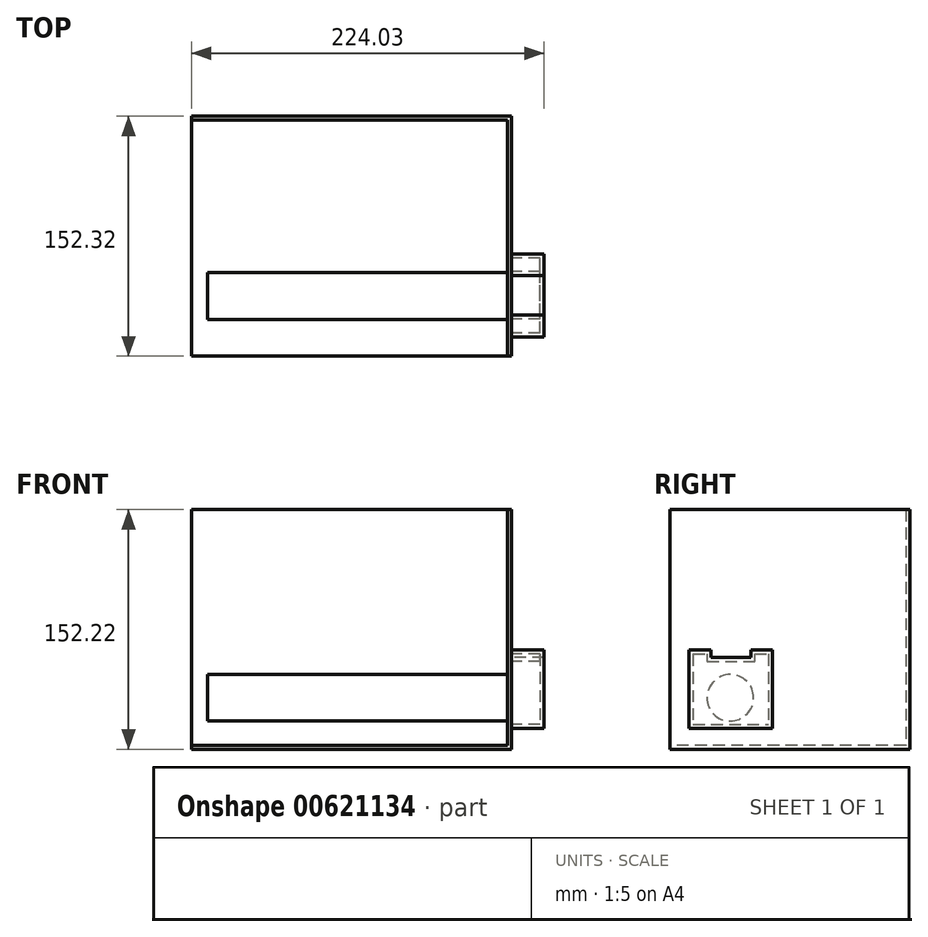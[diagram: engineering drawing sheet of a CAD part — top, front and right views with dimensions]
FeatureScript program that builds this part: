
annotation { "Feature Type Name" : "Feature", "Feature Type Description" : "" }
export const myFeature = defineFeature(function(context is Context, id is Id, definition is map)
    precondition{}
    {
        {
            var Q0;
            Q0=qCreatedBy(makeId("Right.planeOp"),FACE);
            var sketch = newSketch(context, id + "F0", { "sketchPlane" : qUnion([Q0])});
            skLineSegment(sketch, "E0.bottom", {"start": v(76.16, 76.11) * mm, "end": v(-76.16, 76.11) * mm});
            skLineSegment(sketch, "E0.top", {"start": v(76.16, -76.11) * mm, "end": v(-76.16, -76.11) * mm});
            skLineSegment(sketch, "E0.left", {"start": v(76.16, 76.11) * mm, "end": v(76.16, -76.11) * mm});
            skLineSegment(sketch, "E0.right", {"start": v(-76.16, 76.11) * mm, "end": v(-76.16, -76.11) * mm});
            skPoint(sketch, "E0.middle", {"position": v(0, 0) * mm});
            skSolve(sketch);
        }
        {
            var Q0;
            Q0 = qSketchRegion(id + "F0", true);
            extrude(context, id + "F1", {"entities" : qUnion([Q0]), "oppositeDirection" : true, "depth" : 203.2 * mm, "offsetDistance" : 25.4 * mm});
        }
        {
            var Q0;
            Q0=makeQuery(id+"F1.opExtrude","CAP_FACE",FACE,{"disambiguationData":[OSD([sQuery(id+"F0.wireOp",EDGE,"E0.bottom"),sQuery(id+"F0.wireOp",EDGE,"E0.top"),sQuery(id+"F0.wireOp",EDGE,"E0.left"),sQuery(id+"F0.wireOp",EDGE,"E0.right")])],"isStart":true});
            var sketch = newSketch(context, id + "F2", { "sketchPlane" : qUnion([Q0])});
            skLineSegment(sketch, "E1.top", {"start": v(-64.17, -62.88) * mm, "end": v(-11.2, -62.88) * mm});
            skLineSegment(sketch, "E1.left", {"start": v(-64.17, -13.06) * mm, "end": v(-64.17, -62.88) * mm});
            skLineSegment(sketch, "E1.right", {"start": v(-11.2, -13.06) * mm, "end": v(-11.2, -62.88) * mm});
            skLineSegment(sketch, "E2", {"start": v(-64.17, -13.06) * mm, "end": v(-50.1, -13.06) * mm});
            skLineSegment(sketch, "E3", {"start": v(-50.1, -13.06) * mm, "end": v(-50.1, -17.93) * mm});
            skLineSegment(sketch, "E4", {"start": v(-50.1, -17.93) * mm, "end": v(-24.97, -17.93) * mm});
            skLineSegment(sketch, "E5", {"start": v(-24.97, -17.93) * mm, "end": v(-24.97, -13.06) * mm});
            skLineSegment(sketch, "E6", {"start": v(-24.97, -13.06) * mm, "end": v(-11.2, -13.06) * mm});
            skSolve(sketch);
        }
        {
            var Q0;
            Q0=makeQuery(id+"F2.imprint","IMPRINT",FACE,{"disambiguationData":[TD([[makeQuery(id+"F2.imprint","IMPRINT",EDGE,{"derivedFrom":sQuery(id+"F2.wireOp",EDGE,"E1.top")}),1.0]])]});
            extrude(context, id + "F3", {"entities" : qUnion([Q0]), "operationType" : NewBodyOperationType.ADD, "depth" : 20.83 * mm, "offsetDistance" : 25.4 * mm});
        }
        {
            var Q0;
            Q0=makeQuery(id+"F1.opExtrude","SWEPT_FACE",FACE,{"disambiguationData":[OSD([sQuery(id+"F0.wireOp",EDGE,"E0.right")])]});
            var Q1;
            Q1=makeQuery(id+"F1.opExtrude","SWEPT_FACE",FACE,{"disambiguationData":[OSD([sQuery(id+"F0.wireOp",EDGE,"E0.bottom")])]});
            var Q2;
            Q2=makeQuery(id+"F1.opExtrude","CAP_FACE",FACE,{"disambiguationData":[OSD([sQuery(id+"F0.wireOp",EDGE,"E0.bottom"),sQuery(id+"F0.wireOp",EDGE,"E0.top"),sQuery(id+"F0.wireOp",EDGE,"E0.left"),sQuery(id+"F0.wireOp",EDGE,"E0.right")])],"isStart":false});
            shell(context, id + "F4", {"entities" : qUnion([Q0, Q1, Q2]), "thickness" : 2.54 * mm});
        }
        {
            var Q0;
            Q0=makeQuery(id+"F4.opShell","OFFSET_FACE",FACE,{"disambiguationData":[OSD([sQuery(id+"F0.wireOp",EDGE,"E0.bottom"),sQuery(id+"F0.wireOp",EDGE,"E0.top"),sQuery(id+"F0.wireOp",EDGE,"E0.left"),sQuery(id+"F0.wireOp",EDGE,"E0.right")])]});
            var sketch = newSketch(context, id + "F5", { "sketchPlane" : qUnion([Q0])});
            skCircle(sketch, "E7", {"center": v(38, -43.42) * mm, "radius": 14.8 * mm});
            skPoint(sketch, "E7.first.point", {"position": v(37.69, -28.61) * mm});
            skPoint(sketch, "E7.second.point", {"position": v(51.02, -50.47) * mm});
            skPoint(sketch, "E7.third.point", {"position": v(28.24, -54.54) * mm});
            skSolve(sketch);
        }
        {
            var Q0;
            Q0=makeQuery(id+"F5.imprint","IMPRINT",FACE,{"disambiguationData":[TD([[makeQuery(id+"F5.imprint","IMPRINT",EDGE,{"derivedFrom":sQuery(id+"F5.wireOp",EDGE,"E7")}),1.0]])]});
            extrude(context, id + "F6", {"entities" : qUnion([Q0]), "depth" : 190.5 * mm, "offsetDistance" : 25.4 * mm});
        }
    });
